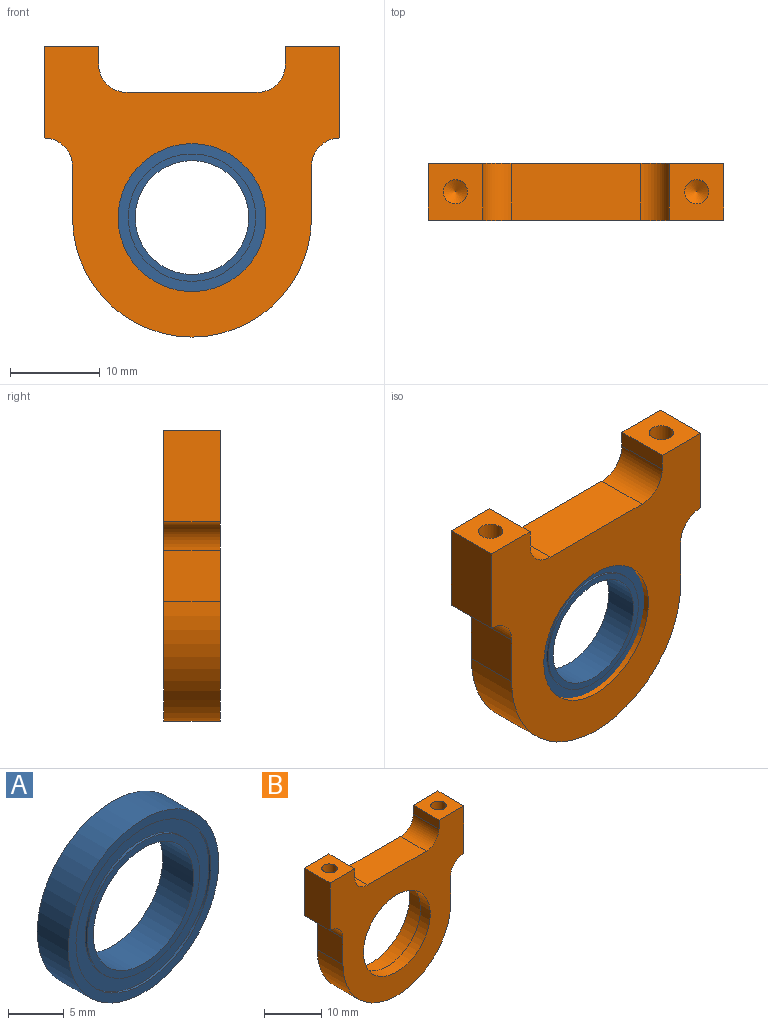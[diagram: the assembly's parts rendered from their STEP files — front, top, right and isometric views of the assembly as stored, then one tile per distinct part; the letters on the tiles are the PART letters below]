
ASSEMBLY  parts=2 mates=1
PART A: 12 faces, bbox 19.1x3.9x19.1 mm
  f0: cylinder r=7.11mm len=14.22mm, axis (0,-1,0), area 11.4mm2, adj f6,f11
  f1: cylinder r=8.55mm len=17.09mm, axis (0,-1,0), area 13.6mm2, adj f9,f11
  f2: cylinder r=7.11mm len=14.22mm, axis (0,1,0), area 11.4mm2, adj f7,f10
  f3: cylinder r=8.55mm len=17.09mm, axis (0,1,0), area 13.6mm2, adj f8,f10
  f4: cylinder r=6.35mm len=12.7mm, axis (0,-1,0), area 156.1mm2, adj f6,f7
  f5: cylinder r=9.53mm len=19.05mm, axis (0,-1,0), area 234.1mm2, adj f8,f9
  f6: plane 14.22x14.22mm, normal (0,-1,0), area 32.2mm2, adj f0,f4
  f7: plane 14.22x14.22mm, normal (0,1,0), area 32.2mm2, adj f2,f4
  f8: plane 19.05x19.05mm, normal (0,1,0), area 55.5mm2, adj f3,f5
  f9: plane 19.05x19.05mm, normal (0,-1,0), area 55.5mm2, adj f1,f5
  f10: plane 17.09x17.09mm, normal (0,1,0), area 70.6mm2, adj f2,f3
  f11: plane 17.09x17.09mm, normal (0,-1,0), area 70.6mm2, adj f0,f1
PART B: 23 faces, bbox 33x6.4x32.4 mm
  f0: cylinder r=8.26mm len=16.51mm, axis (0,1,0), area 123.8mm2, adj f17,f22
  f1: cylinder r=9.53mm len=19.05mm, axis (0,1,0), area 237.1mm2, adj f16,f22
  f2: cylinder r=1.35mm len=7.62mm, axis (0,0,1), area 64.8mm2, adj f3,f9
  f3: cone r=1.35mm half-angle=59deg, axis (0,0,1), area 6.7mm2, adj f2
  f4: cylinder r=1.35mm len=7.62mm, axis (0,0,1), area 64.8mm2, adj f5,f13
  f5: cone r=1.35mm half-angle=59deg, axis (0,0,1), area 6.7mm2, adj f4
  f6: cylinder r=13.33mm len=26.67mm, axis (0,-1,0), area 266mm2, adj f7,f15,f16,f17
  f7: plane 6.35x5.72mm, normal (-1,0,0), area 36.3mm2, adj f6,f16,f17,f18
  f8: plane 10.16x6.35mm, normal (-1,0,0), area 64.5mm2, adj f9,f16,f17,f18
  f9: plane 6.35x6.08mm, normal (0,0,1), area 32.9mm2, adj f2,f8,f10,f16,f17
  f10: plane 6.35x1.91mm, normal (1,0,0), area 12.1mm2, adj f9,f16,f17,f21
  f11: plane 14.51x6.35mm, normal (0,0,1), area 92.1mm2, adj f16,f17,f20,f21
  f12: plane 6.35x1.91mm, normal (-1,0,0), area 12.1mm2, adj f13,f16,f17,f20
  f13: plane 6.35x6.08mm, normal (0,0,1), area 32.9mm2, adj f4,f12,f14,f16,f17
  f14: plane 10.16x6.35mm, normal (1,0,0), area 64.5mm2, adj f13,f16,f17,f19
  f15: plane 6.35x5.72mm, normal (1,0,0), area 36.3mm2, adj f6,f16,f17,f19
  f16: plane 33.02x32.39mm, normal (0,1,0), area 469.6mm2, adj f1,f6,f7,f8,f9,f10,f11,f12
  f17: plane 33.02x32.39mm, normal (0,-1,0), area 540.5mm2, adj f0,f6,f7,f8,f9,f10,f11,f12
  f18: cylinder r=3.17mm len=6.35mm, axis (0,1,0), area 31.7mm2, adj f7,f8,f16,f17
  f19: cylinder r=3.17mm len=6.35mm, axis (0,1,0), area 31.7mm2, adj f14,f15,f16,f17
  f20: cylinder r=3.17mm len=6.35mm, axis (0,1,0), area 31.7mm2, adj f11,f12,f16,f17
  f21: cylinder r=3.17mm len=6.35mm, axis (0,1,0), area 31.7mm2, adj f10,f11,f16,f17
  f22: plane 19.05x19.05mm, normal (0,1,0), area 70.9mm2, adj f0,f1
PLACE A t=(0,0.43,0)mm
PLACE B at identity
MATE fastened A.f0 <-> B.f0  axis (0,-1,0) through (0,2.39,0)mm
